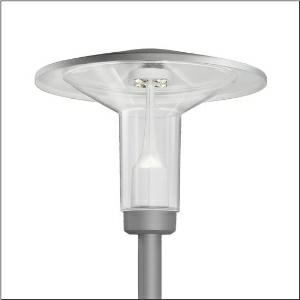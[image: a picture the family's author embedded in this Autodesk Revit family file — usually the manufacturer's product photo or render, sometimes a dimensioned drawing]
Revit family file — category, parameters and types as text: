
# Revit family: laterne_iq___p1_0a_5xa5255bf14h_d88c
name_source: partatom
category: Lighting Fixtures
units: mm (PartAtom-declared; Revit-internal decimal feet)

## family parameters
Cut with Voids When Loaded = No
Host = Face
Light Source = No
Part Type = Normal
Room Calculation Point = No
Round Connector Dimension = Use Diameter
Shared = No

## types (1)
- --- (1 x LED, 1510 lm, 12.9 W, 2200K)
    Apparent Load = 13 VA
    CIE Flux Codes = 35 64 91 96 100
    Color Rendering = 70
    Color Temperature = 2200K
    Default Elevation = 1800 mm
    Description = Lantern iQ, mast luminaire, Module 540 iQ-SR, primary light control with 3 zone facetted reflector, of plastic, silver coated, highly specular, structured, primary optical cover: cover, of PMMA, transparent, light distribution: P1.0a, light emission: direct distribution, primary light characteristic: strongly asymmetric, installation type: post-top, LED, High Power LED, rated luminous flux: 1.510lm, luminous efficacy: 117lm/W, light colour: 722, colour temperature: 2200K, control gear: iQ Street-Remote, control: pre-setting: logarithmic dimming characteristic, Street-Remote, Auto-Match, Temp-Guard, Lumen-Switch, Night-Set, Smart-Wire, Light-Fading, Desk-Remote (wireless, voltage-free reading and setting of iQ features in the workshop via application-optimized NFC function/RFID function), optimised constant luminous flux control (CLO 2.0), with terminal, 6-pole, max. 2.5mm², mains connection: 230..240V, AC, 50/60Hz, start of lifetime: 13W, end of service life: 13W, reduction: 6W, luminaire housing, upper part, of glass-fibre reinforced polyester, coated, Siteco® metallic grey (DB 702S), diameter: 750mm, height: 583mm, spigot size: d x l = 76 x 70mm (post-top) | with reducer (optional accessory) 60 x 70mm, mounting height: 3..5m, post-top mast mounting element, of diecast aluminium, coated, Siteco® metallic grey (DB 702S), Module 540 iQ-SR, traffic white (RAL 9016), equipment: standard, protection rating (complete): IP65, insulation class (complete): insulation class II (safety insulation), certification: CE, ENEC, VDE, packaging unit: 1 piece

Light Distribution: P1.0a
    Height = 583 mm
    Lamp = 1 x LED
    Lamp Light Flux = 1510 lm
    Lamp Power = 12.9 W
    Lamp count = 1
    Length = 750 mm
    Luminous efficacy = 117 lm/W
    Manufacturer = Siteco
    ModVariant = No
    Model = 5XA5255BF14H
    Number of Poles = 1
    OnlyDefault = Yes
    Power Factor = 1
    Product Name = Laterne iQ | P1.0a
    Product group = mast luminaire | pylon top
    ProductGroupID = 6100
    Protection Class = Protection class II
    Protection Degree = IP 65
    RLX_Detail_Level = 1
    RLX_Emergency_Light_Flux = 0 lm
    RLX_Emergency_Type = 0
    RLX_Emergency_Type_DB = No
    RlxData = <blob elided: 74137 chars, md5=c95af331>
    Socket = socket
    Standby Power = 0 W
    System Light Flux = 1510 lm
    System Power = 13 W
    Type Comments = factory setting: luminous flux: 100 % | dim-lin: 254 | 516 mA
    Type Image = l_1006050.jpg
    URL = http://relux.com
    VarID = @adj_160015
    Voltage = 0 V
    Weight = 0.00 kg
    Width = 0 mm  [stored 0 ft]

note: [stored X ft] marks values corroborated as IEEE doubles in the binary element streams (Revit-internal decimal feet)

## geometry (parser evidence)
native form markers: Blend x4, Sweep x9
no freeform markers — native parametric forms only
